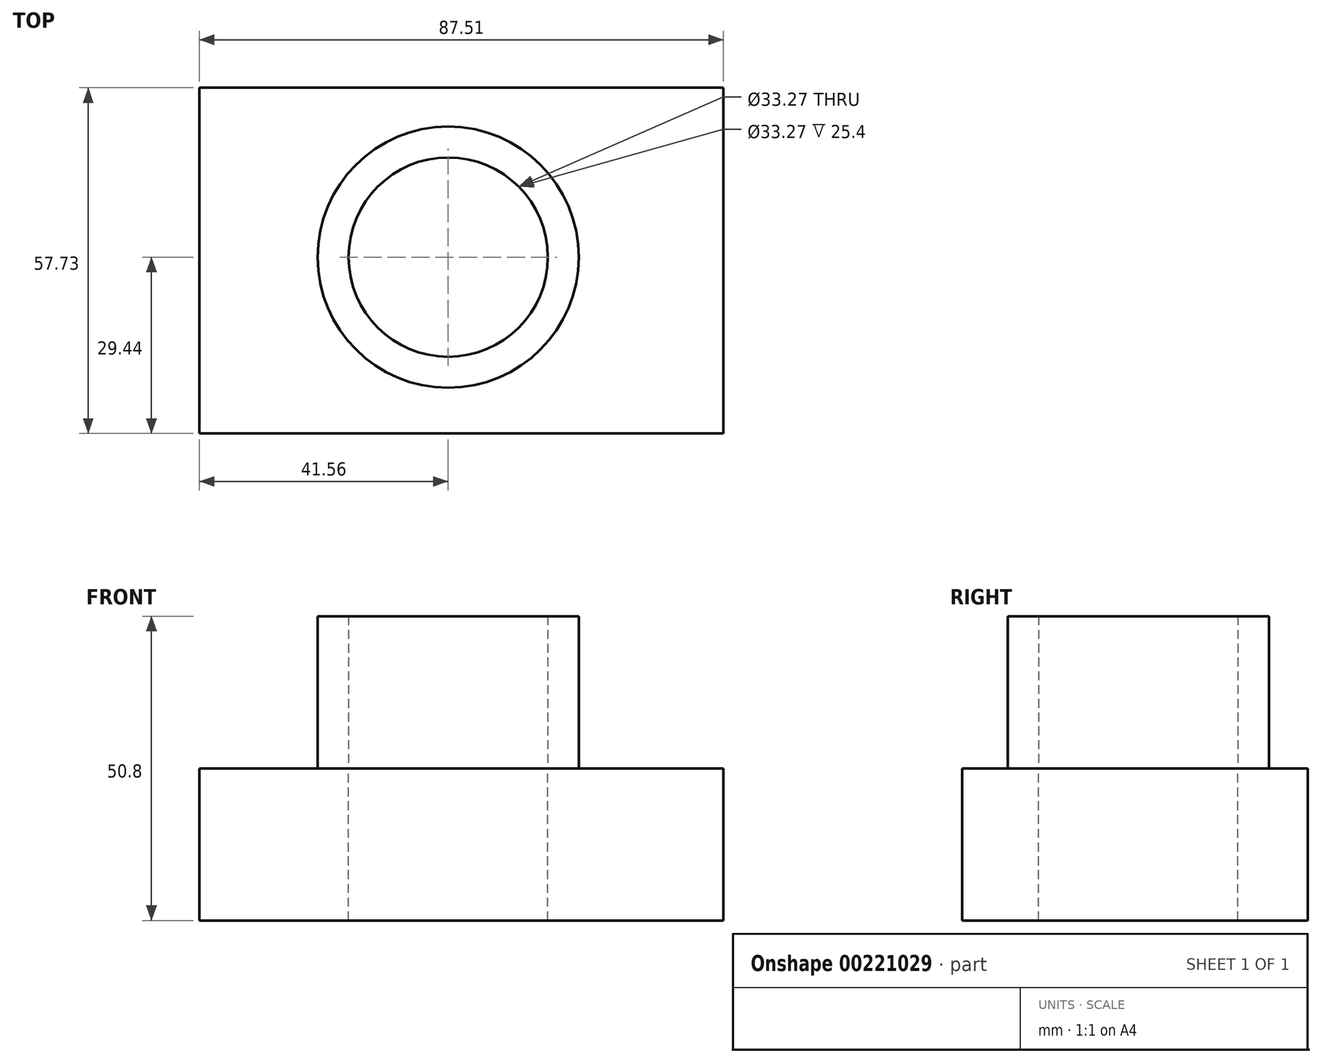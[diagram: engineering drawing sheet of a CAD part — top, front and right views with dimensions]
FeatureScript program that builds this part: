
annotation { "Feature Type Name" : "Feature", "Feature Type Description" : "" }
export const myFeature = defineFeature(function(context is Context, id is Id, definition is map)
    precondition{}
    {
        {
            var Q0;
            Q0=qCreatedBy(makeId("Top.planeOp"),FACE);
            var sketch = newSketch(context, id + "F0", { "sketchPlane" : qUnion([Q0])});
            skLineSegment(sketch, "E0.bottom", {"start": v(-41.56, 28.29) * mm, "end": v(45.95, 28.29) * mm});
            skLineSegment(sketch, "E0.top", {"start": v(-41.56, -29.44) * mm, "end": v(45.95, -29.44) * mm});
            skLineSegment(sketch, "E0.left", {"start": v(-41.56, 28.29) * mm, "end": v(-41.56, -29.44) * mm});
            skLineSegment(sketch, "E0.right", {"start": v(45.95, 28.29) * mm, "end": v(45.95, -29.44) * mm});
            skSolve(sketch);
        }
        {
            var Q0;
            Q0 = qSketchRegion(id + "F0", true);
            extrude(context, id + "F1", {"entities" : qUnion([Q0]), "depth" : 25.4 * mm});
        }
        {
            var Q0;
            Q0=makeQuery(id+"F1.opExtrude","CAP_FACE",FACE,{"disambiguationData":[OSD([sQuery(id+"F0.wireOp",EDGE,"E0.bottom"),sQuery(id+"F0.wireOp",EDGE,"E0.top"),sQuery(id+"F0.wireOp",EDGE,"E0.left"),sQuery(id+"F0.wireOp",EDGE,"E0.right")])],"isStart":false});
            var sketch = newSketch(context, id + "F2", { "sketchPlane" : qUnion([Q0])});
            skCircle(sketch, "E1", {"center": v(0, 0) * mm, "radius": 16.64 * mm});
            skSolve(sketch);
        }
        {
            var Q0;
            Q0 = qSketchRegion(id + "F2", true);
            extrude(context, id + "F3", {"entities" : qUnion([Q0]), "operationType" : NewBodyOperationType.REMOVE, "oppositeDirection" : true, "depth" : 25.4 * mm});
        }
        {
            var Q0;
            Q0=makeQuery(id+"F1.opExtrude","CAP_FACE",FACE,{"disambiguationData":[OSD([sQuery(id+"F0.wireOp",EDGE,"E0.bottom"),sQuery(id+"F0.wireOp",EDGE,"E0.top"),sQuery(id+"F0.wireOp",EDGE,"E0.left"),sQuery(id+"F0.wireOp",EDGE,"E0.right")])],"isStart":false});
            var sketch = newSketch(context, id + "F4", { "sketchPlane" : qUnion([Q0])});
            skCircle(sketch, "E2", {"center": v(0, 0) * mm, "radius": 21.8 * mm});
            skSolve(sketch);
        }
        {
            var Q0;
            Q0 = qSketchRegion(id + "F4", true);
            extrude(context, id + "F5", {"entities" : qUnion([Q0]), "operationType" : NewBodyOperationType.ADD, "depth" : 25.4 * mm});
        }
        {
            var Q0;
            Q0=makeQuery(id+"F1.opExtrude","CAP_FACE",FACE,{"disambiguationData":[OSD([sQuery(id+"F0.wireOp",EDGE,"E0.bottom"),sQuery(id+"F0.wireOp",EDGE,"E0.top"),sQuery(id+"F0.wireOp",EDGE,"E0.left"),sQuery(id+"F0.wireOp",EDGE,"E0.right")])],"isStart":true});
            var sketch = newSketch(context, id + "F6", { "sketchPlane" : qUnion([Q0])});
            skCircle(sketch, "E3", {"center": v(0, 0) * mm, "radius": 16.63 * mm});
            skSolve(sketch);
        }
        {
            var Q0;
            Q0 = qSketchRegion(id + "F6", true);
            extrude(context, id + "F7", {"entities" : qUnion([Q0]), "operationType" : NewBodyOperationType.REMOVE, "oppositeDirection" : true, "depth" : 68.83 * mm});
        }
    });
